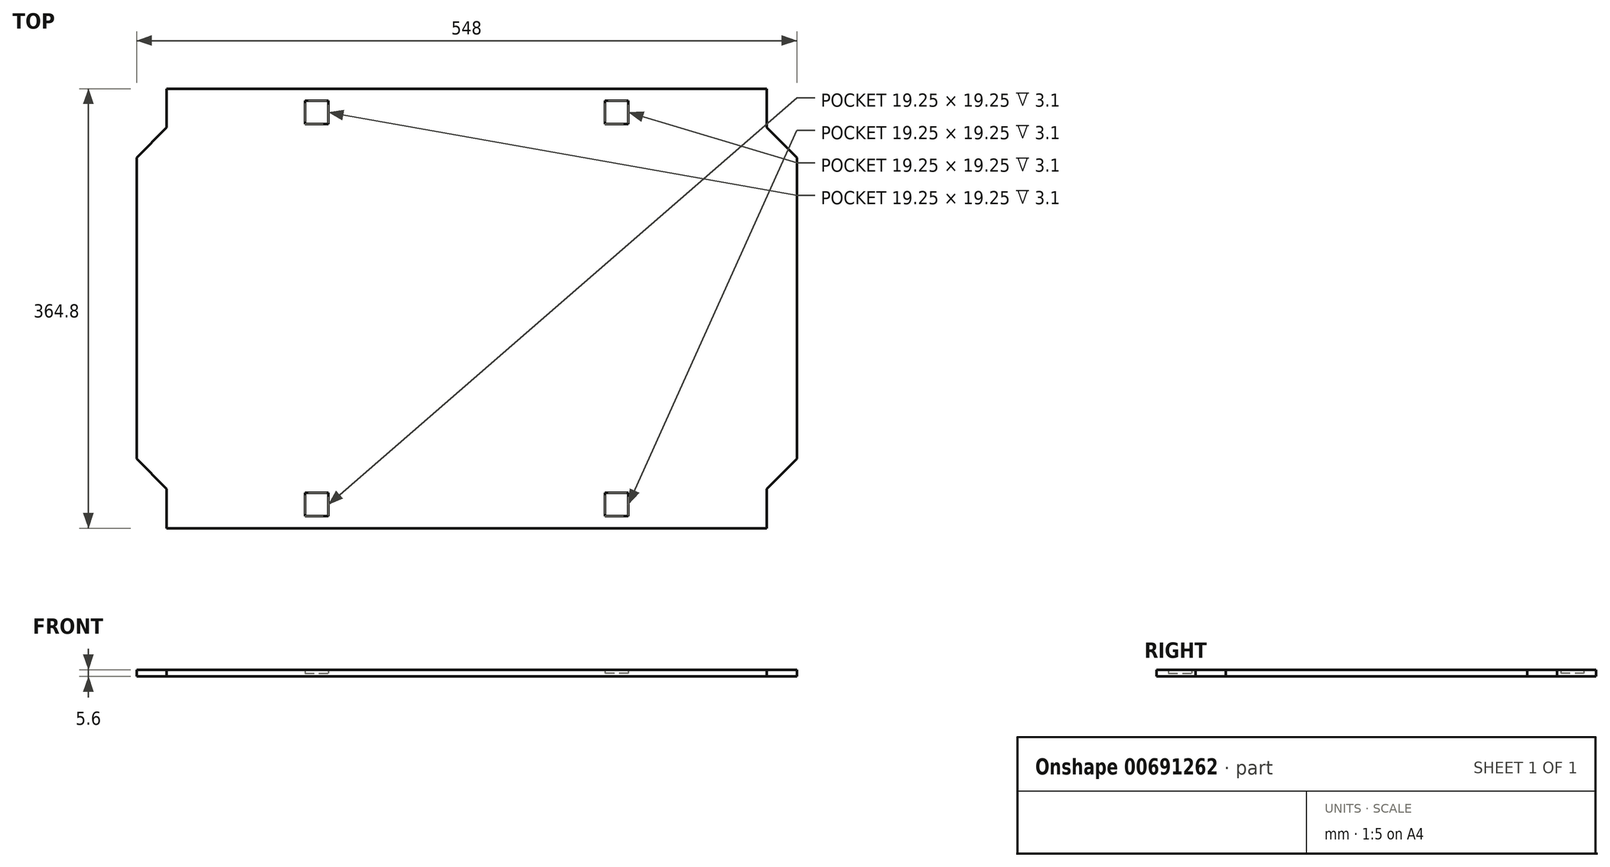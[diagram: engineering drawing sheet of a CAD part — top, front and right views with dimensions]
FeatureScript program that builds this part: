
annotation { "Feature Type Name" : "Feature", "Feature Type Description" : "" }
export const myFeature = defineFeature(function(context is Context, id is Id, definition is map)
    precondition{}
    {
        {
            var Q0;
            Q0=qCreatedBy(makeId("Top.planeOp"),FACE);
            var sketch = newSketch(context, id + "F0", { "sketchPlane" : qUnion([Q0])});
            skLineSegment(sketch, "E0.bottom", {"start": v(-297.48, 203) * mm, "end": v(297.48, 203) * mm, "construction": true});
            skLineSegment(sketch, "E0.top", {"start": v(-297.48, -203) * mm, "end": v(297.48, -203) * mm, "construction": true});
            skLineSegment(sketch, "E0.left", {"start": v(-297.48, 203) * mm, "end": v(-297.48, -203) * mm, "construction": true});
            skLineSegment(sketch, "E0.right", {"start": v(297.48, 203) * mm, "end": v(297.48, -203) * mm, "construction": true});
            skLineSegment(sketch, "E1.left", {"start": v(-249, 182.4) * mm, "end": v(-249, 150.15) * mm});
            skLineSegment(sketch, "E1.right", {"start": v(249, 182.4) * mm, "end": v(249, 150.15) * mm});
            skLineSegment(sketch, "E2", {"start": v(-274, 125.15) * mm, "end": v(-274, -124.85) * mm});
            skLineSegment(sketch, "E3", {"start": v(-274, 125.15) * mm, "end": v(-249, 150.15) * mm});
            skLineSegment(sketch, "E4", {"start": v(-274, -124.85) * mm, "end": v(-249, -149.85) * mm});
            skLineSegment(sketch, "E5", {"start": v(274, 125.15) * mm, "end": v(249, 150.15) * mm});
            skLineSegment(sketch, "E6", {"start": v(274, 125.15) * mm, "end": v(274, -124.85) * mm});
            skLineSegment(sketch, "E7", {"start": v(274, -124.85) * mm, "end": v(249, -149.85) * mm});
            skLineSegment(sketch, "E8.trimOffspring", {"start": v(-249, -149.85) * mm, "end": v(-249, -182.4) * mm});
            skLineSegment(sketch, "E9", {"start": v(249, -149.85) * mm, "end": v(249, -182.4) * mm});
            skLineSegment(sketch, "E10", {"start": v(0, 0) * mm, "end": v(0, -124.92) * mm, "construction": true});
            skLineSegment(sketch, "E11", {"start": v(0, 175.15) * mm, "end": v(0, 156.08) * mm, "construction": true});
            skPoint(sketch, "E12.orphan", {"position": v(249, 175.15) * mm});
            skLineSegment(sketch, "E13", {"start": v(-124.5, 175.15) * mm, "end": v(-124.5, 131.15) * mm, "construction": true});
            skPoint(sketch, "E14.oppositeSnap0", {"position": v(-124.5, 153.15) * mm});
            skLineSegment(sketch, "E14.bottom", {"start": v(-134.12, 172.4) * mm, "end": v(-114.88, 172.4) * mm});
            skLineSegment(sketch, "E14.top", {"start": v(-134.12, 153.15) * mm, "end": v(-114.88, 153.15) * mm});
            skLineSegment(sketch, "E14.left", {"start": v(-134.13, 172.4) * mm, "end": v(-134.13, 153.15) * mm});
            skLineSegment(sketch, "E14.right", {"start": v(-114.88, 172.4) * mm, "end": v(-114.88, 153.15) * mm});
            skLineSegment(sketch, "E15.MirrorCS", {"start": v(114.88, 172.4) * mm, "end": v(114.88, 153.15) * mm});
            skLineSegment(sketch, "E16.MirrorCS", {"start": v(134.12, 172.4) * mm, "end": v(114.88, 172.4) * mm});
            skLineSegment(sketch, "E17.MirrorCS", {"start": v(134.12, 153.15) * mm, "end": v(114.88, 153.15) * mm});
            skLineSegment(sketch, "E18.MirrorCS", {"start": v(134.13, 172.4) * mm, "end": v(134.13, 153.15) * mm});
            skLineSegment(sketch, "E19", {"start": v(0, 0) * mm, "end": v(137.8, 0) * mm, "construction": true});
            skLineSegment(sketch, "E20.MirrorCS", {"start": v(134.13, -172.4) * mm, "end": v(134.13, -153.15) * mm});
            skLineSegment(sketch, "E21.MirrorCS", {"start": v(134.12, -172.4) * mm, "end": v(114.88, -172.4) * mm});
            skLineSegment(sketch, "E22.MirrorCS", {"start": v(134.12, -153.15) * mm, "end": v(114.88, -153.15) * mm});
            skLineSegment(sketch, "E23.MirrorCS", {"start": v(114.88, -172.4) * mm, "end": v(114.88, -153.15) * mm});
            skLineSegment(sketch, "E24.MirrorCS", {"start": v(-134.12, -153.15) * mm, "end": v(-114.87, -153.15) * mm});
            skLineSegment(sketch, "E25.MirrorCS", {"start": v(-114.88, -172.4) * mm, "end": v(-114.88, -153.15) * mm});
            skLineSegment(sketch, "E26.MirrorCS", {"start": v(-134.12, -172.4) * mm, "end": v(-114.87, -172.4) * mm});
            skLineSegment(sketch, "E27.MirrorCS", {"start": v(-134.13, -172.4) * mm, "end": v(-134.13, -153.15) * mm});
            skLineSegment(sketch, "E28", {"start": v(-249, 182.4) * mm, "end": v(249, 182.4) * mm});
            skPoint(sketch, "E1.bottom.start.orphan", {"position": v(-249, 200.15) * mm});
            skPoint(sketch, "E29.orphan", {"position": v(249, 200.15) * mm});
            skLineSegment(sketch, "E30", {"start": v(-249, -182.4) * mm, "end": v(249, -182.4) * mm});
            skPoint(sketch, "E1.top.start.orphan", {"position": v(-249, -199.85) * mm});
            skPoint(sketch, "E31.orphan", {"position": v(249, -199.85) * mm});
            skSolve(sketch);
        }
        {
            var Q0;
            Q0 = qSketchRegion(id + "F0", true);
            extrude(context, id + "F1", {"entities" : qUnion([Q0]), "depth" : 5.6 * mm, "offsetDistance" : 25 * mm});
        }
        {
            var Q0;
            Q0=makeQuery(id+"F1.opExtrude","CAP_FACE",FACE,{"disambiguationData":[OSD([sQuery(id+"F0.wireOp",EDGE,"E1.left"),sQuery(id+"F0.wireOp",EDGE,"E1.right"),sQuery(id+"F0.wireOp",EDGE,"E2"),sQuery(id+"F0.wireOp",EDGE,"E3"),sQuery(id+"F0.wireOp",EDGE,"E4"),sQuery(id+"F0.wireOp",EDGE,"E5"),sQuery(id+"F0.wireOp",EDGE,"E6"),sQuery(id+"F0.wireOp",EDGE,"E7"),sQuery(id+"F0.wireOp",EDGE,"E8.trimOffspring"),sQuery(id+"F0.wireOp",EDGE,"E9"),sQuery(id+"F0.wireOp",EDGE,"E14.bottom"),sQuery(id+"F0.wireOp",EDGE,"E14.top"),sQuery(id+"F0.wireOp",EDGE,"E14.left"),sQuery(id+"F0.wireOp",EDGE,"E14.right"),sQuery(id+"F0.wireOp",EDGE,"E15.MirrorCS"),sQuery(id+"F0.wireOp",EDGE,"E16.MirrorCS"),sQuery(id+"F0.wireOp",EDGE,"E17.MirrorCS"),sQuery(id+"F0.wireOp",EDGE,"E18.MirrorCS"),sQuery(id+"F0.wireOp",EDGE,"E20.MirrorCS"),sQuery(id+"F0.wireOp",EDGE,"E21.MirrorCS"),sQuery(id+"F0.wireOp",EDGE,"E22.MirrorCS"),sQuery(id+"F0.wireOp",EDGE,"E23.MirrorCS"),sQuery(id+"F0.wireOp",EDGE,"E24.MirrorCS"),sQuery(id+"F0.wireOp",EDGE,"E25.MirrorCS"),sQuery(id+"F0.wireOp",EDGE,"E26.MirrorCS"),sQuery(id+"F0.wireOp",EDGE,"E27.MirrorCS"),sQuery(id+"F0.wireOp",EDGE,"E28"),sQuery(id+"F0.wireOp",EDGE,"E30")])],"isStart":true});
            var sketch = newSketch(context, id + "F2", { "sketchPlane" : qUnion([Q0])});
            skLineSegment(sketch, "E32.0", {"start": v(-134.12, 153.15) * mm, "end": v(-114.87, 153.15) * mm});
            skLineSegment(sketch, "E33.0", {"start": v(-114.88, 172.4) * mm, "end": v(-114.88, 153.15) * mm});
            skLineSegment(sketch, "E34.0", {"start": v(-134.12, 172.4) * mm, "end": v(-114.88, 172.4) * mm});
            skLineSegment(sketch, "E35.0", {"start": v(-134.13, 172.4) * mm, "end": v(-134.13, 153.15) * mm});
            skLineSegment(sketch, "E36.0", {"start": v(134.13, 172.4) * mm, "end": v(114.88, 172.4) * mm});
            skLineSegment(sketch, "E37.0", {"start": v(114.88, 172.4) * mm, "end": v(114.88, 153.15) * mm});
            skLineSegment(sketch, "E38.0", {"start": v(134.13, 153.15) * mm, "end": v(114.88, 153.15) * mm});
            skLineSegment(sketch, "E39.0", {"start": v(134.13, 172.4) * mm, "end": v(134.13, 153.15) * mm});
            skLineSegment(sketch, "E40.0", {"start": v(134.12, -153.15) * mm, "end": v(114.88, -153.15) * mm});
            skLineSegment(sketch, "E41.0", {"start": v(134.13, -172.4) * mm, "end": v(134.13, -153.15) * mm});
            skLineSegment(sketch, "E42.0", {"start": v(134.13, -172.4) * mm, "end": v(114.88, -172.4) * mm});
            skLineSegment(sketch, "E43.0", {"start": v(114.88, -172.4) * mm, "end": v(114.88, -153.15) * mm});
            skLineSegment(sketch, "E44.0", {"start": v(-114.88, -172.4) * mm, "end": v(-114.88, -153.15) * mm});
            skLineSegment(sketch, "E45.0", {"start": v(-134.12, -172.4) * mm, "end": v(-114.88, -172.4) * mm});
            skLineSegment(sketch, "E46.0", {"start": v(-134.13, -172.4) * mm, "end": v(-134.13, -153.15) * mm});
            skLineSegment(sketch, "E47.0", {"start": v(-134.13, -153.15) * mm, "end": v(-114.88, -153.15) * mm});
            skSolve(sketch);
        }
        {
            var Q0;
            Q0 = qSketchRegion(id + "F2", true);
            extrude(context, id + "F3", {"entities" : qUnion([Q0]), "operationType" : NewBodyOperationType.ADD, "oppositeDirection" : true, "depth" : 2.5 * mm, "offsetDistance" : 25 * mm});
        }
    });
